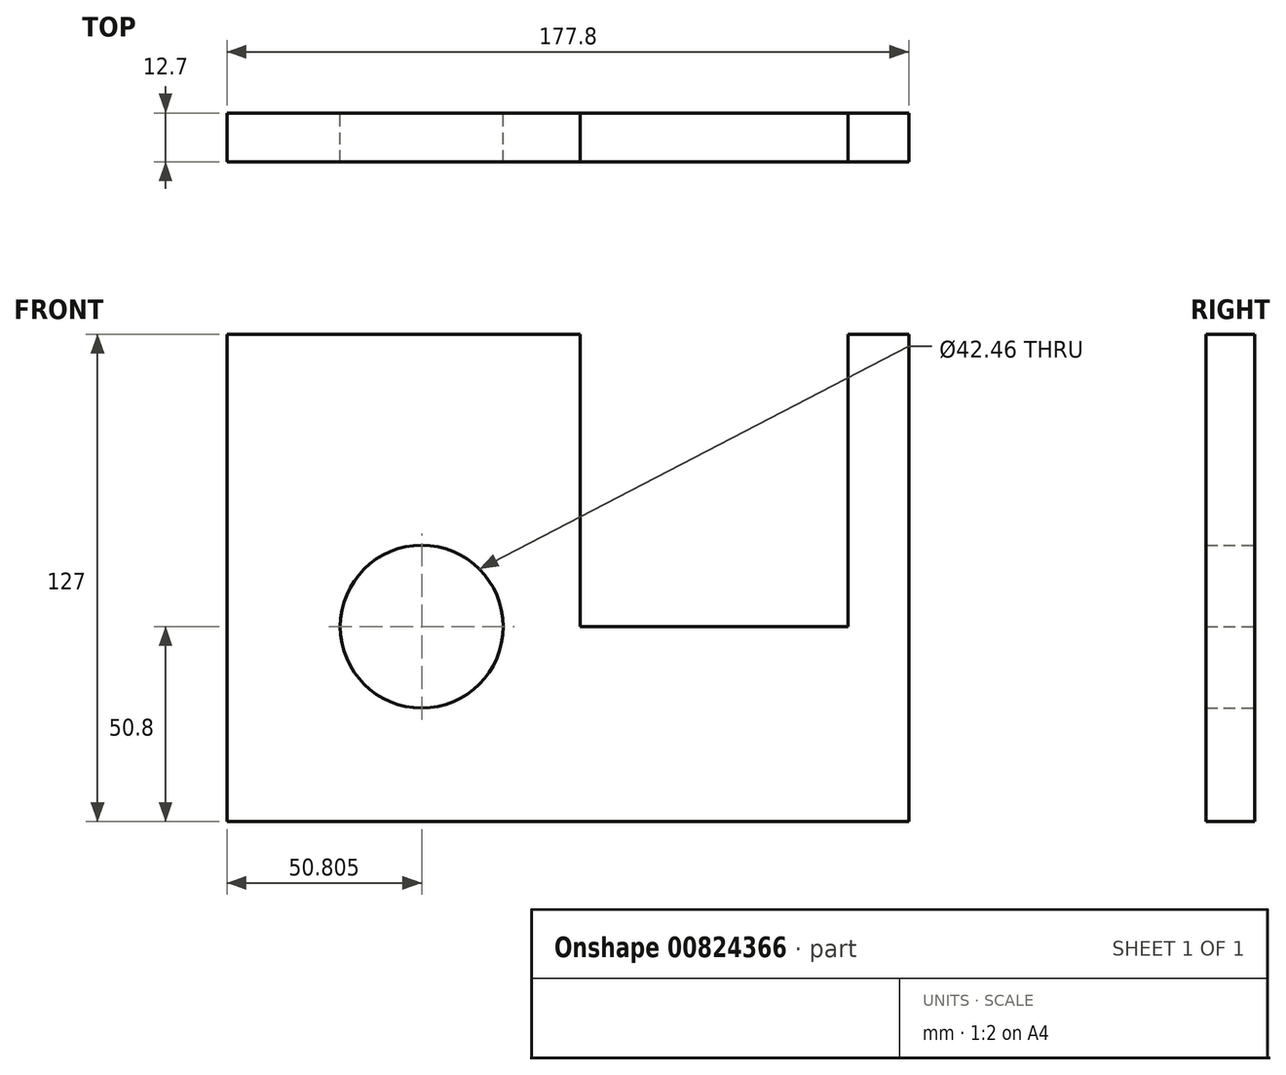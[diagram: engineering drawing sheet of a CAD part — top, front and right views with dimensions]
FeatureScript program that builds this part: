
annotation { "Feature Type Name" : "Feature", "Feature Type Description" : "" }
export const myFeature = defineFeature(function(context is Context, id is Id, definition is map)
    precondition{}
    {
        {
            var Q0;
            Q0=qCreatedBy(makeId("Front.planeOp"),FACE);
            var sketch = newSketch(context, id + "F0", { "sketchPlane" : qUnion([Q0])});
            skLineSegment(sketch, "E0", {"start": v(-92.08, 76.2) * mm, "end": v(-92.07, -50.8) * mm});
            skLineSegment(sketch, "E1", {"start": v(-92.07, -50.8) * mm, "end": v(85.73, -50.8) * mm});
            skLineSegment(sketch, "E2", {"start": v(85.73, -50.8) * mm, "end": v(85.73, 76.2) * mm});
            skLineSegment(sketch, "E3", {"start": v(85.73, 76.2) * mm, "end": v(69.85, 76.2) * mm});
            skLineSegment(sketch, "E4", {"start": v(69.85, 76.2) * mm, "end": v(69.85, 0) * mm});
            skLineSegment(sketch, "E5", {"start": v(-92.07, 76.2) * mm, "end": v(0, 76.2) * mm});
            skLineSegment(sketch, "E6", {"start": v(0, 76.2) * mm, "end": v(0, 0) * mm});
            skLineSegment(sketch, "E7", {"start": v(69.85, 0) * mm, "end": v(0, 0) * mm});
            skCircle(sketch, "E8", {"center": v(-41.27, 0) * mm, "radius": 21.23 * mm});
            skSolve(sketch);
        }
        {
            var Q0;
            Q0 = qSketchRegion(id + "F0", true);
            extrude(context, id + "F1", {"entities" : qUnion([Q0]), "depth" : 12.7 * mm, "offsetDistance" : 25.4 * mm});
        }
    });
